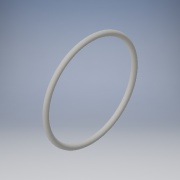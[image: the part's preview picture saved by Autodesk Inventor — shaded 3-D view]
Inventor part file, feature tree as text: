
AUTODESK INVENTOR PART (.ipt)
format: ipt  version: 2016 (Build 200138000, 138)  size: 116,736 bytes
history: native  units: in
note: dims shown in document units (in); Inventor stores cm internally (conversion verified against a paired STEP export)
features: revolve x1, sketch x1
ambient origin geometry x8: Origin, YZ Plane, XZ Plane, XY Plane, X Axis, Y Axis, Z Axis, Center Point
bodies: Solid1 (feature_tree)
feature tree (2):
  revolve  "Revolution1"  [1 undecoded]
  sketch  "Sketch1"  dims[d0=0.105in d1=0.925in d2=90.0deg]
note: 1 required parameter value undecoded (feature->parameter linkage not recoverable at this tier; creation-order binding heuristic only, values carry confidence <= 0.55)
